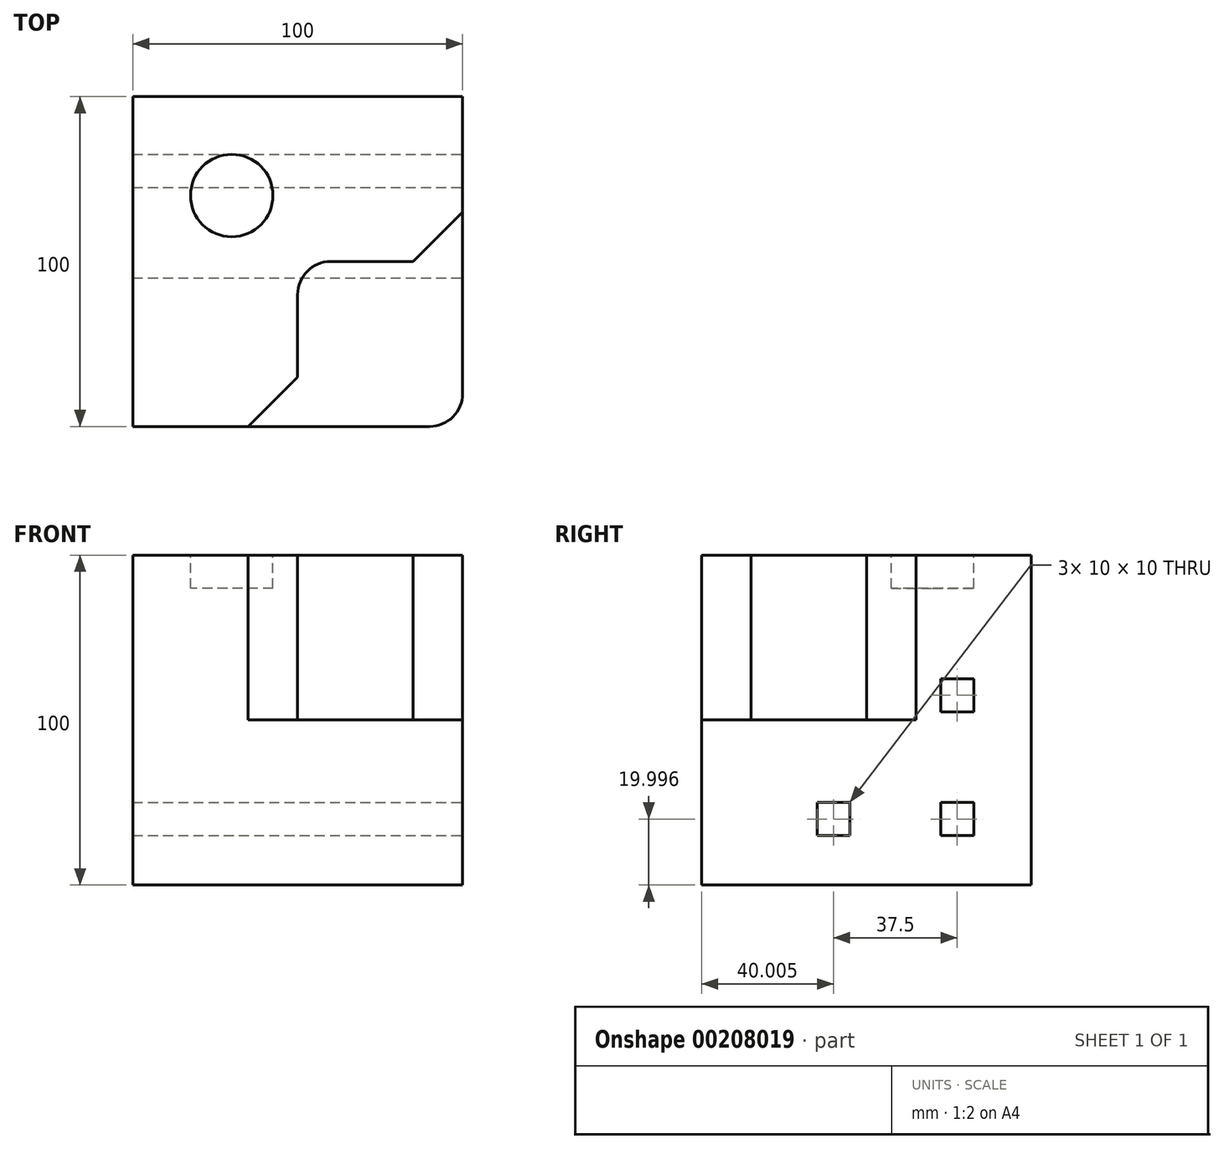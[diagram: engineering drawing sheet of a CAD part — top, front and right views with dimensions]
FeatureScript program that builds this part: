
annotation { "Feature Type Name" : "Feature", "Feature Type Description" : "" }
export const myFeature = defineFeature(function(context is Context, id is Id, definition is map)
    precondition{}
    {
        {
            var Q0;
            Q0=qCreatedBy(makeId("Right.planeOp"),FACE);
            var sketch = newSketch(context, id + "F0", { "sketchPlane" : qUnion([Q0])});
            skLineSegment(sketch, "E0", {"start": v(66.84, 68.3) * mm, "end": v(-33.16, 68.3) * mm});
            skLineSegment(sketch, "E1", {"start": v(66.84, 68.3) * mm, "end": v(66.84, -31.7) * mm});
            skLineSegment(sketch, "E2", {"start": v(-33.16, 68.3) * mm, "end": v(-33.16, 33.3) * mm});
            skLineSegment(sketch, "E3", {"start": v(66.84, -31.7) * mm, "end": v(31.84, -31.7) * mm});
            skLineSegment(sketch, "E4", {"start": v(31.84, -31.7) * mm, "end": v(16.84, -16.7) * mm});
            skLineSegment(sketch, "E5", {"start": v(-33.16, 33.3) * mm, "end": v(-18.16, 18.3) * mm});
            skLineSegment(sketch, "E6", {"start": v(-18.16, 18.3) * mm, "end": v(6.84, 18.3) * mm});
            skLineSegment(sketch, "E7", {"start": v(16.84, 8.3) * mm, "end": v(16.84, -16.7) * mm});
            skPoint(sketch, "E8.visualSharp", {"position": v(16.84, 18.3) * mm});
            skArc(sketch, "E8.filletArc", {"start": v(16.84, 8.3) * mm, "mid": v(13.92, 15.37) * mm, "end": v(6.84, 18.3) * mm});
            skLineSegment(sketch, "E9", {"start": v(-33.16, 68.3) * mm, "end": v(-33.16, -21.7) * mm});
            skLineSegment(sketch, "E10", {"start": v(-23.16, -31.7) * mm, "end": v(66.84, -31.7) * mm});
            skPoint(sketch, "E11.visualSharp", {"position": v(-33.16, -31.7) * mm});
            skArc(sketch, "E11.filletArc", {"start": v(-33.16, -21.7) * mm, "mid": v(-30.23, -28.78) * mm, "end": v(-23.16, -31.7) * mm});
            skSolve(sketch);
        }
        {
            var Q0;
            Q0=makeQuery(id+"F0.imprint","IMPRINT",FACE,{"disambiguationData":[TD([[makeQuery(id+"F0.imprint","IMPRINT",EDGE,{"derivedFrom":sQuery(id+"F0.wireOp",EDGE,"E0")}),1.0]])]});
            extrude(context, id + "F1", {"entities" : qUnion([Q0]), "depth" : 50 * mm});
        }
        {
            var Q0;
            Q0=makeQuery(id+"F1.opExtrude","CAP_FACE",FACE,{"disambiguationData":[OSD([sQuery(id+"F0.wireOp",EDGE,"E0"),sQuery(id+"F0.wireOp",EDGE,"E1"),sQuery(id+"F0.wireOp",EDGE,"E4"),sQuery(id+"F0.wireOp",EDGE,"E5"),sQuery(id+"F0.wireOp",EDGE,"E6"),sQuery(id+"F0.wireOp",EDGE,"E7"),sQuery(id+"F0.wireOp",EDGE,"E8.filletArc"),sQuery(id+"F0.wireOp",EDGE,"E9"),sQuery(id+"F0.wireOp",EDGE,"E10")])],"isStart":true});
            var Q1;
            Q1 = qSketchRegion(id + "F0", true);
            extrude(context, id + "F2", {"entities" : qUnion([Q0, Q1]), "operationType" : NewBodyOperationType.ADD, "depth" : 50 * mm});
        }
        {
            var Q0;
            Q0=makeQuery(id+"F1.opExtrude","CAP_FACE",FACE,{"disambiguationData":[OSD([sQuery(id+"F0.wireOp",EDGE,"E0"),sQuery(id+"F0.wireOp",EDGE,"E1"),sQuery(id+"F0.wireOp",EDGE,"E4"),sQuery(id+"F0.wireOp",EDGE,"E5"),sQuery(id+"F0.wireOp",EDGE,"E6"),sQuery(id+"F0.wireOp",EDGE,"E7"),sQuery(id+"F0.wireOp",EDGE,"E8.filletArc"),sQuery(id+"F0.wireOp",EDGE,"E9"),sQuery(id+"F0.wireOp",EDGE,"E10")])],"isStart":false});
            var sketch = newSketch(context, id + "F3", { "sketchPlane" : qUnion([Q0])});
            skCircle(sketch, "E12", {"center": v(36.84, 38.3) * mm, "radius": 12.5 * mm});
            skSolve(sketch);
        }
        {
            var Q0;
            Q0 = qSketchRegion(id + "F3", true);
            extrude(context, id + "F4", {"entities" : qUnion([Q0]), "operationType" : NewBodyOperationType.ADD, "oppositeDirection" : true, "depth" : 10 * mm});
        }
        {
            var Q0;
            Q0 = qSketchRegion(id + "F3", true);
            extrude(context, id + "F5", {"entities" : qUnion([Q0]), "operationType" : NewBodyOperationType.REMOVE, "oppositeDirection" : true, "depth" : 10 * mm});
        }
        {
            var Q0;
            {var subQ0=sQuery(id+"F0.wireOp",EDGE,"E10");var subQ1=makeQuery(id+"F0.imprint","INTERSECT",VERTEX,{"derivedFrom":[sQuery(id+"F0.wireOp",EDGE,"E4"),subQ0]});Q0=makeQuery(id+"F2.boolean.opBoolean","MERGE",FACE,{"derivedFrom":[makeQuery(id+"F1.opExtrude","SWEPT_FACE",FACE,{"disambiguationData":[OSD([subQ0])]}),makeQuery(id+"F2.opExtrude","SWEPT_FACE",FACE,{"disambiguationData":[OSD([subQ0]),TDD([makeQuery(id+"F0.imprint","IMPRINT",EDGE,{"disambiguationData":[TD([[subQ1,1.0]])],"derivedFrom":subQ0}),makeQuery(id+"F0.imprint","IMPRINT",EDGE,{"disambiguationData":[TD([[makeQuery(id+"F0.imprint","INTERSECT",VERTEX,{"derivedFrom":[sQuery(id+"F0.wireOp",EDGE,"E1"),subQ0]}),1.0]])],"derivedFrom":subQ0})])]})]});}
            var sketch = newSketch(context, id + "F6", { "sketchPlane" : qUnion([Q0])});
            skLineSegment(sketch, "E13.bottom", {"start": v(-25, -39.34) * mm, "end": v(-35, -39.34) * mm});
            skLineSegment(sketch, "E13.top", {"start": v(-25, -49.34) * mm, "end": v(-35, -49.34) * mm});
            skLineSegment(sketch, "E13.left", {"start": v(-25, -39.34) * mm, "end": v(-25, -49.34) * mm});
            skLineSegment(sketch, "E13.right", {"start": v(-35, -39.34) * mm, "end": v(-35, -49.34) * mm});
            skLineSegment(sketch, "E14.0.1.0", {"start": v(-25, -1.84) * mm, "end": v(-25, -11.84) * mm});
            skLineSegment(sketch, "E14.0.1.1", {"start": v(-25, -11.84) * mm, "end": v(-35, -11.84) * mm});
            skLineSegment(sketch, "E14.0.1.2", {"start": v(-25, -1.84) * mm, "end": v(-35, -1.84) * mm});
            skLineSegment(sketch, "E14.0.1.3", {"start": v(-35, -1.84) * mm, "end": v(-35, -11.84) * mm});
            skLineSegment(sketch, "E14.1.0.0", {"start": v(12.5, -39.34) * mm, "end": v(12.5, -49.34) * mm});
            skLineSegment(sketch, "E14.1.0.1", {"start": v(12.5, -49.34) * mm, "end": v(2.5, -49.34) * mm});
            skLineSegment(sketch, "E14.1.0.2", {"start": v(12.5, -39.34) * mm, "end": v(2.5, -39.34) * mm});
            skLineSegment(sketch, "E14.1.0.3", {"start": v(2.5, -39.34) * mm, "end": v(2.5, -49.34) * mm});
            skLineSegment(sketch, "E14.direction1", {"start": v(-35, -49.34) * mm, "end": v(2.5, -49.34) * mm, "construction": true});
            skLineSegment(sketch, "E14.direction2", {"start": v(-35, -49.34) * mm, "end": v(-35, -11.84) * mm, "construction": true});
            skSolve(sketch);
        }
        {
            var Q0;
            Q0=makeQuery(id+"F6.imprint","IMPRINT",FACE,{"disambiguationData":[TD([[makeQuery(id+"F6.imprint","IMPRINT",EDGE,{"derivedFrom":sQuery(id+"F6.wireOp",EDGE,"E14.0.1.0")}),-1.0]])]});
            extrude(context, id + "F7", {"entities" : qUnion([Q0]), "operationType" : NewBodyOperationType.REMOVE, "oppositeDirection" : true, "depth" : 100 * mm});
        }
        {
            var Q0;
            Q0=makeQuery(id+"F6.imprint","IMPRINT",FACE,{"disambiguationData":[TD([[makeQuery(id+"F6.imprint","IMPRINT",EDGE,{"derivedFrom":sQuery(id+"F6.wireOp",EDGE,"E14.1.0.0")}),-1.0]])]});
            extrude(context, id + "F8", {"entities" : qUnion([Q0]), "operationType" : NewBodyOperationType.REMOVE, "oppositeDirection" : true, "depth" : 100 * mm});
        }
        {
            var Q0;
            Q0=makeQuery(id+"F6.imprint","IMPRINT",FACE,{"disambiguationData":[TD([[makeQuery(id+"F6.imprint","IMPRINT",EDGE,{"derivedFrom":sQuery(id+"F6.wireOp",EDGE,"E13.bottom")}),1.0]])]});
            extrude(context, id + "F9", {"entities" : qUnion([Q0]), "operationType" : NewBodyOperationType.REMOVE, "oppositeDirection" : true, "depth" : 100 * mm});
        }
        {
            var Q0;
            Q0=makeQuery(id+"F1.opExtrude","SWEPT_BODY",BODY,{"disambiguationData":[OSD([sQuery(id+"F0.wireOp",EDGE,"E0"),sQuery(id+"F0.wireOp",EDGE,"E1"),sQuery(id+"F0.wireOp",EDGE,"E4"),sQuery(id+"F0.wireOp",EDGE,"E5"),sQuery(id+"F0.wireOp",EDGE,"E6"),sQuery(id+"F0.wireOp",EDGE,"E7"),sQuery(id+"F0.wireOp",EDGE,"E8.filletArc"),sQuery(id+"F0.wireOp",EDGE,"E9"),sQuery(id+"F0.wireOp",EDGE,"E10")])]});
            transform(context, id + "F10", {"entities" : qUnion([Q0]), "transformType" : TransformType.TRANSLATION_3D, "dx" : 25 * mm, "dy" : 60 * mm, "dz" : 0 * mm, "makeCopy" : false});
        }
        {
            var Q0;
            Q0=makeQuery(id+"F1.opExtrude","SWEPT_BODY",BODY,{"disambiguationData":[OSD([sQuery(id+"F0.wireOp",EDGE,"E0"),sQuery(id+"F0.wireOp",EDGE,"E1"),sQuery(id+"F0.wireOp",EDGE,"E4"),sQuery(id+"F0.wireOp",EDGE,"E5"),sQuery(id+"F0.wireOp",EDGE,"E6"),sQuery(id+"F0.wireOp",EDGE,"E7"),sQuery(id+"F0.wireOp",EDGE,"E8.filletArc"),sQuery(id+"F0.wireOp",EDGE,"E9"),sQuery(id+"F0.wireOp",EDGE,"E10")])]});
            var Q1;
            {var subQ0=sQuery(id+"F0.wireOp",EDGE,"E0");Q1=makeQuery(id+"F2.opExtrude","CAP_EDGE",EDGE,{"disambiguationData":[OSD([subQ0]),TDD([makeQuery(id+"F0.imprint","IMPRINT",EDGE,{"derivedFrom":subQ0})])],"isStart":false});}
            transform(context, id + "F11", {"entities" : qUnion([Q0]), "transformType" : TransformType.ROTATION, "transformAxis" : qUnion([Q1]), "angle" : 90 * degree, "makeCopy" : false});
        }
        {
            var Q0;
            Q0=makeQuery(id+"F1.opExtrude","SWEPT_BODY",BODY,{"disambiguationData":[OSD([sQuery(id+"F0.wireOp",EDGE,"E0"),sQuery(id+"F0.wireOp",EDGE,"E1"),sQuery(id+"F0.wireOp",EDGE,"E4"),sQuery(id+"F0.wireOp",EDGE,"E5"),sQuery(id+"F0.wireOp",EDGE,"E6"),sQuery(id+"F0.wireOp",EDGE,"E7"),sQuery(id+"F0.wireOp",EDGE,"E8.filletArc"),sQuery(id+"F0.wireOp",EDGE,"E9"),sQuery(id+"F0.wireOp",EDGE,"E10")])]});
            transform(context, id + "F12", {"entities" : qUnion([Q0]), "transformType" : TransformType.TRANSLATION_3D, "dx" : 25 * mm, "dy" : -25 * mm, "dz" : -70 * mm, "makeCopy" : false});
        }
        {
            var Q0;
            Q0=makeQuery(id+"F1.opExtrude","SWEPT_BODY",BODY,{"disambiguationData":[OSD([sQuery(id+"F0.wireOp",EDGE,"E0"),sQuery(id+"F0.wireOp",EDGE,"E1"),sQuery(id+"F0.wireOp",EDGE,"E4"),sQuery(id+"F0.wireOp",EDGE,"E5"),sQuery(id+"F0.wireOp",EDGE,"E6"),sQuery(id+"F0.wireOp",EDGE,"E7"),sQuery(id+"F0.wireOp",EDGE,"E8.filletArc"),sQuery(id+"F0.wireOp",EDGE,"E9"),sQuery(id+"F0.wireOp",EDGE,"E10")])]});
            transform(context, id + "F13", {"entities" : qUnion([Q0]), "transformType" : TransformType.TRANSLATION_3D, "dx" : -1.5 * mm, "dy" : 0 * mm, "dz" : 0 * mm, "makeCopy" : false});
        }
    });
